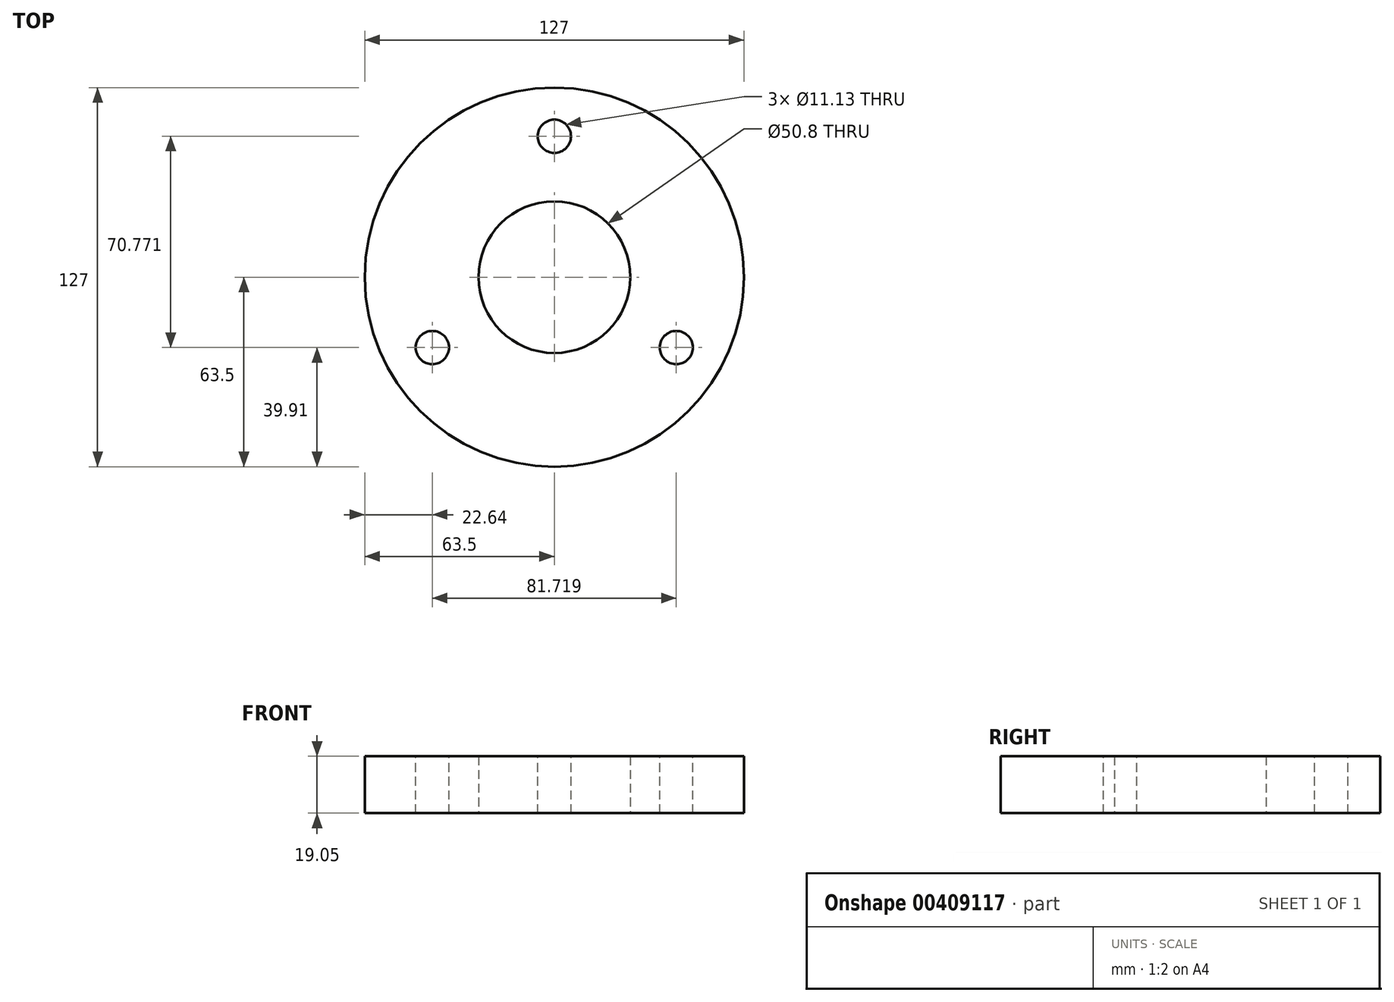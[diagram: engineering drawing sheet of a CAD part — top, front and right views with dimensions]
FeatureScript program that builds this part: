
annotation { "Feature Type Name" : "Feature", "Feature Type Description" : "" }
export const myFeature = defineFeature(function(context is Context, id is Id, definition is map)
    precondition{}
    {
        {
            var Q0;
            Q0=qCreatedBy(makeId("Top.planeOp"),FACE);
            var sketch = newSketch(context, id + "F0", { "sketchPlane" : qUnion([Q0])});
            skCircle(sketch, "E0", {"center": v(0, 0) * mm, "radius": 63.5 * mm});
            skCircle(sketch, "E1", {"center": v(0, 0) * mm, "radius": 25.4 * mm});
            skSolve(sketch);
        }
        {
            var Q0;
            Q0 = qSketchRegion(id + "F0", true);
            extrude(context, id + "F1", {"entities" : qUnion([Q0]), "depth" : 19.05 * mm});
        }
        {
            var Q0;
            Q0=makeQuery(id+"F1.opExtrude","CAP_FACE",FACE,{"disambiguationData":[OSD([sQuery(id+"F0.wireOp",EDGE,"E0"),sQuery(id+"F0.wireOp",EDGE,"E1")])],"isStart":false});
            var sketch = newSketch(context, id + "F2", { "sketchPlane" : qUnion([Q0])});
            skCircle(sketch, "E2", {"center": v(0, 0) * mm, "radius": 47.18 * mm, "construction": true});
            skCircle(sketch, "E3", {"center": v(0, 47.18) * mm, "radius": 5.57 * mm});
            skCircle(sketch, "E4", {"center": v(-40.86, -23.6) * mm, "radius": 5.57 * mm});
            skCircle(sketch, "E5", {"center": v(40.86, -23.6) * mm, "radius": 5.57 * mm});
            skLineSegment(sketch, "E6", {"start": v(0, 0) * mm, "end": v(-40.86, -23.6) * mm, "construction": true});
            skLineSegment(sketch, "E7", {"start": v(0, 0) * mm, "end": v(40.86, -23.6) * mm, "construction": true});
            skLineSegment(sketch, "E8", {"start": v(0, 0) * mm, "end": v(0, -56.55) * mm, "construction": true});
            skSolve(sketch);
        }
        {
            var Q0;
            Q0 = qSketchRegion(id + "F2", true);
            extrude(context, id + "F3", {"entities" : qUnion([Q0]), "operationType" : NewBodyOperationType.REMOVE, "oppositeDirection" : true, "depth" : 25.4 * mm});
        }
    });
